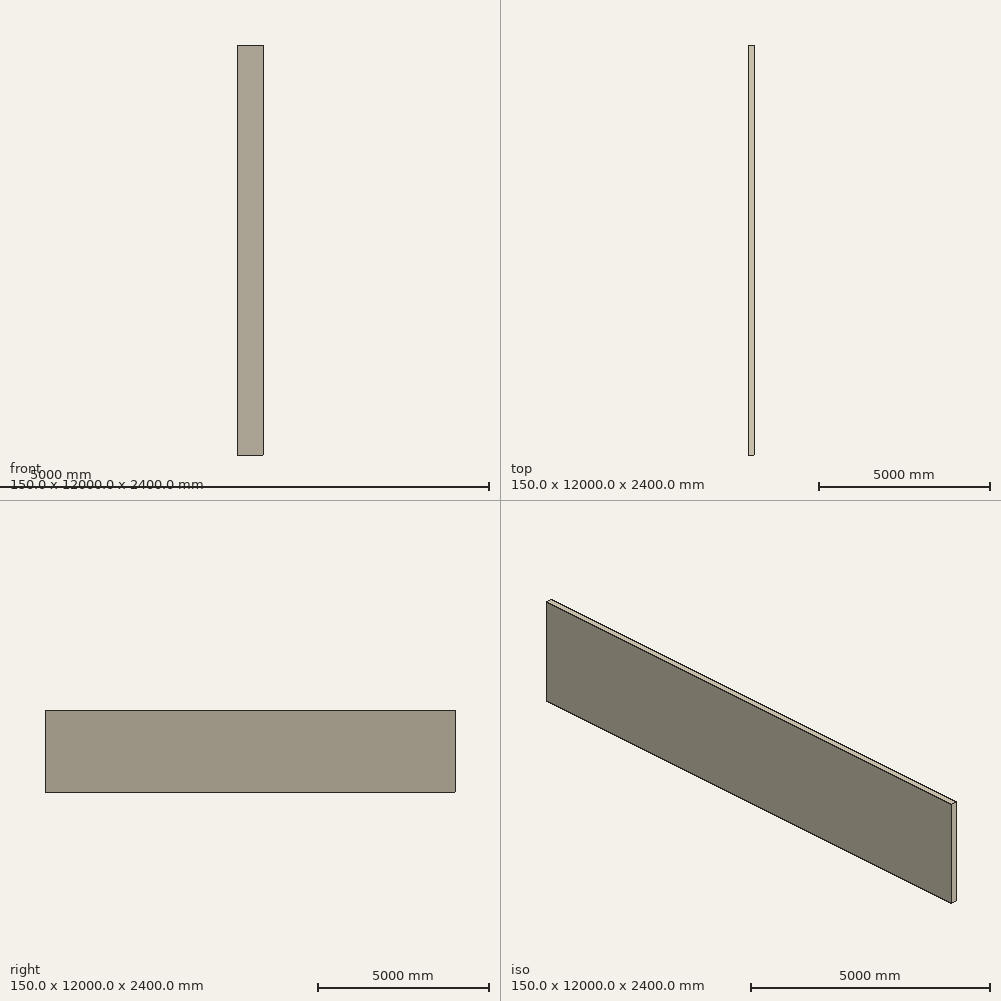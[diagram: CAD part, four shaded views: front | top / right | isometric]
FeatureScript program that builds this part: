
annotation { "Feature Type Name" : "Feature", "Feature Type Description" : "" }
export const myFeature = defineFeature(function(context is Context, id is Id, definition is map)
    precondition{}
    {
        {
            var Q0;
            Q0=qCreatedBy(makeId("Right.planeOp"),FACE);
            var sketch = newSketch(context, id + "F0", { "sketchPlane" : qUnion([Q0])});
            skLineSegment(sketch, "E0.bottom", {"start": v(-11928.93, 2389.15) * mm, "end": v(71.07, 2389.15) * mm});
            skLineSegment(sketch, "E0.top", {"start": v(-11928.93, -10.85) * mm, "end": v(71.07, -10.85) * mm});
            skLineSegment(sketch, "E0.left", {"start": v(-11928.93, 2389.15) * mm, "end": v(-11928.93, -10.85) * mm});
            skLineSegment(sketch, "E0.right", {"start": v(71.07, 2389.15) * mm, "end": v(71.07, -10.85) * mm});
            skSolve(sketch);
        }
        {
            var Q0;
            Q0=makeQuery(id+"F0.imprint","IMPRINT",FACE,{"disambiguationData":[TD([[makeQuery(id+"F0.imprint","IMPRINT",EDGE,{"derivedFrom":sQuery(id+"F0.wireOp",EDGE,"E0.bottom")}),-1.0]])]});
            extrude(context, id + "F1", {"entities" : qUnion([Q0]), "depth" : 150 * mm, "offsetDistance" : 25 * mm});
        }
    });
